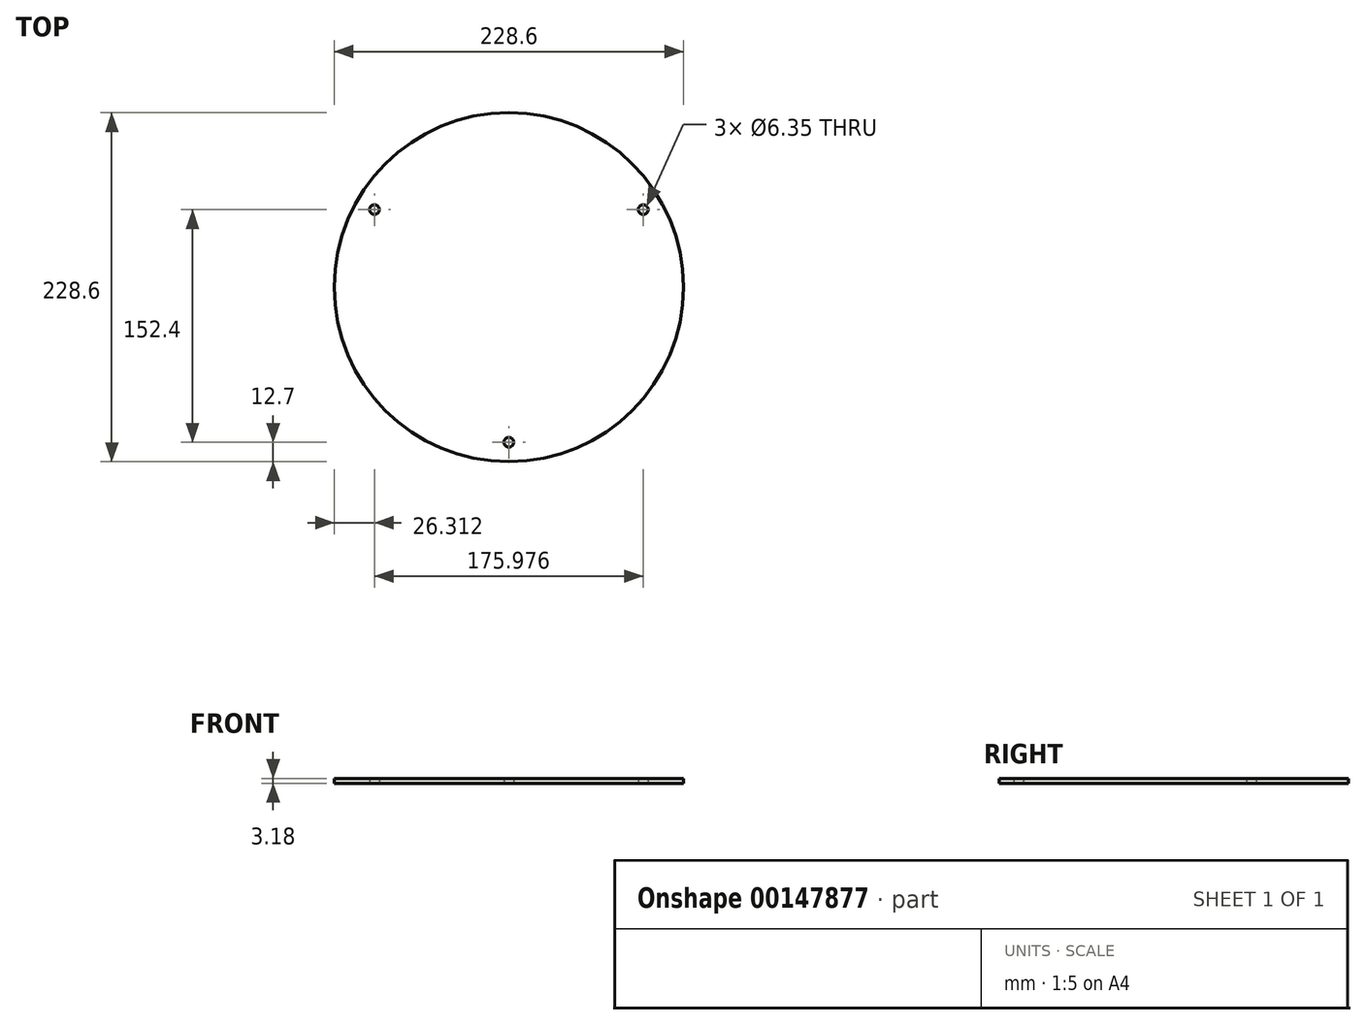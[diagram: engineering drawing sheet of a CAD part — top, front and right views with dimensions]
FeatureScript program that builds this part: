
annotation { "Feature Type Name" : "Feature", "Feature Type Description" : "" }
export const myFeature = defineFeature(function(context is Context, id is Id, definition is map)
    precondition{}
    {
        {
            var Q0;
            Q0=qCreatedBy(makeId("Top.planeOp"),FACE);
            var sketch = newSketch(context, id + "F0", { "sketchPlane" : qUnion([Q0])});
            skPoint(sketch, "E0.middle", {"position": v(0, 0) * mm});
            skCircle(sketch, "E1", {"center": v(0, 0) * mm, "radius": 114.3 * mm});
            skCircle(sketch, "E2.cCircle", {"center": v(0, 0) * mm, "radius": 50.8 * mm, "construction": true});
            skLineSegment(sketch, "E2.0", {"start": v(-87.99, 50.8) * mm, "end": v(87.99, 50.8) * mm, "construction": true});
            skLineSegment(sketch, "E2.1", {"start": v(87.99, 50.8) * mm, "end": v(0, -101.6) * mm, "construction": true});
            skLineSegment(sketch, "E2.2", {"start": v(0, -101.6) * mm, "end": v(-87.99, 50.8) * mm, "construction": true});
            skPoint(sketch, "E2.0.midPoint", {"position": v(0, 50.8) * mm});
            skCircle(sketch, "E3", {"center": v(-87.99, 50.8) * mm, "radius": 12.7 * mm, "construction": true});
            skCircle(sketch, "E4", {"center": v(-87.99, 50.8) * mm, "radius": 3.18 * mm});
            skCircle(sketch, "E5", {"center": v(87.99, 50.8) * mm, "radius": 3.18 * mm});
            skCircle(sketch, "E6", {"center": v(0, -101.6) * mm, "radius": 3.18 * mm});
            skSolve(sketch);
        }
        {
            var Q0;
            Q0=makeQuery(id+"F0.imprint","IMPRINT",FACE,{"disambiguationData":[TD([[makeQuery(id+"F0.imprint","IMPRINT",EDGE,{"derivedFrom":sQuery(id+"F0.wireOp",EDGE,"d7zeTPih-CRss-xDOh-gPdP-rmPCdwzH7cdN.left")}),1.0]])]});
            var Q1;
            Q1=makeQuery(id+"F0.imprint","IMPRINT",FACE,{"disambiguationData":[TD([[makeQuery(id+"F0.imprint","IMPRINT",EDGE,{"derivedFrom":sQuery(id+"F0.wireOp",EDGE,"Jn2k36ax-03Sc-YTBV-3rcB-fQozdpyuW2kT")}),1.0]])]});
            var Q2;
            Q2=makeQuery(id+"F0.imprint","IMPRINT",FACE,{"disambiguationData":[TD([[makeQuery(id+"F0.imprint","IMPRINT",EDGE,{"derivedFrom":sQuery(id+"F0.wireOp",EDGE,"E1")}),1.0]])]});
            extrude(context, id + "F1", {"entities" : qUnion([Q0, Q1, Q2]), "depth" : 3.17 * mm});
        }
    });
